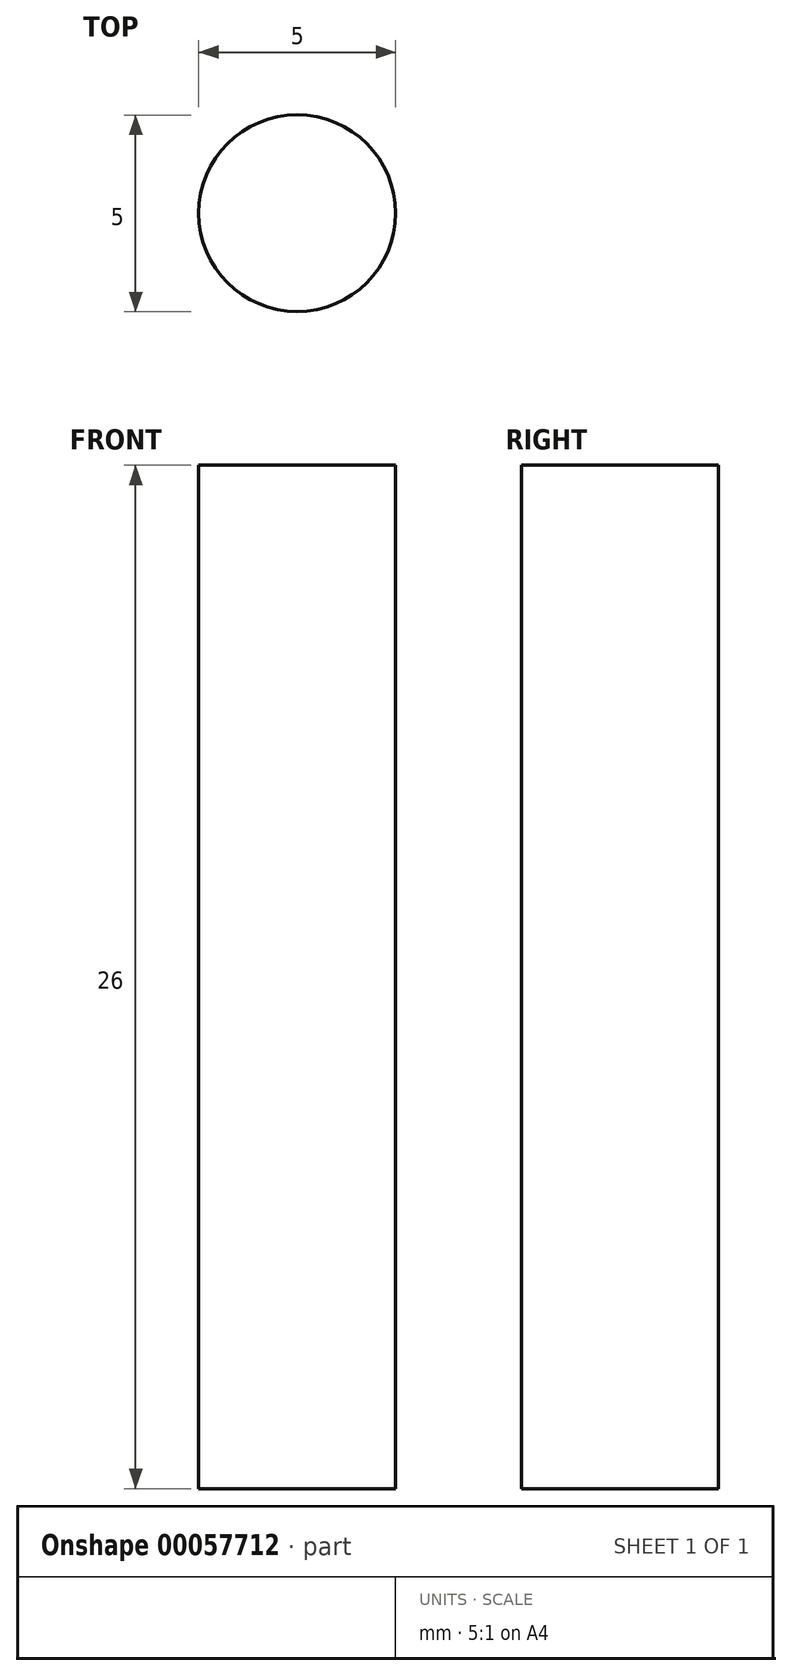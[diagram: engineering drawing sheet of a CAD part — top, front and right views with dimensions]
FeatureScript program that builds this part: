
annotation { "Feature Type Name" : "Feature", "Feature Type Description" : "" }
export const myFeature = defineFeature(function(context is Context, id is Id, definition is map)
    precondition{}
    {
        {
            var Q0;
            Q0=qCreatedBy(makeId("Top.planeOp"),FACE);
            var sketch = newSketch(context, id + "F0", { "sketchPlane" : qUnion([Q0])});
            skCircle(sketch, "E0", {"center": v(0, -0.22) * mm, "radius": 2.5 * mm});
            skSolve(sketch);
        }
        {
            var Q0;
            Q0 = qSketchRegion(id + "F0", true);
            extrude(context, id + "F1", {"entities" : qUnion([Q0]), "depth" : 26 * mm});
        }
    });
